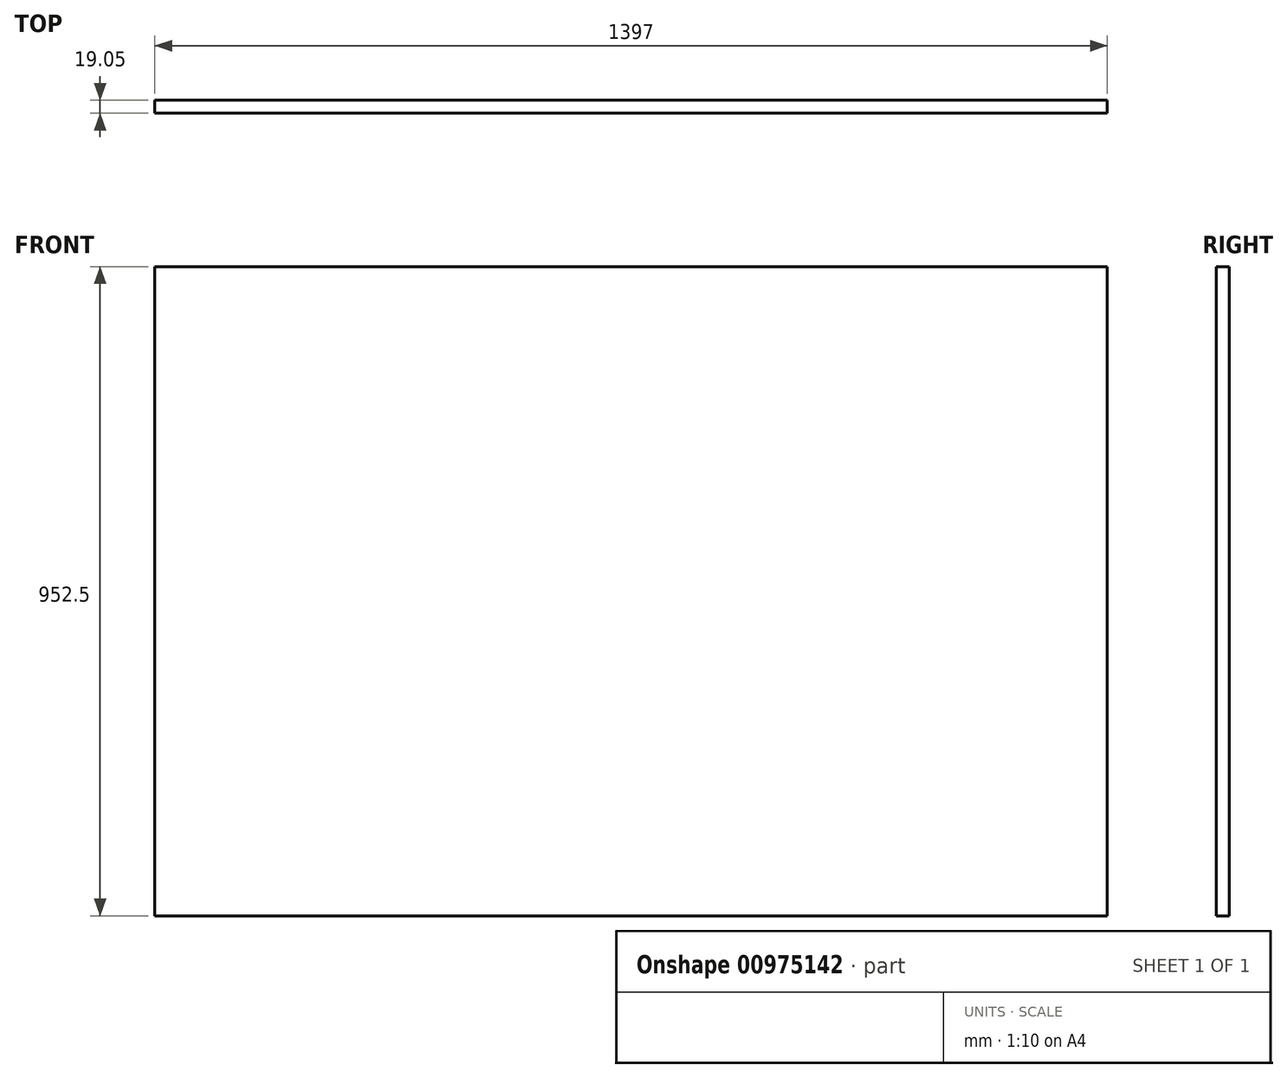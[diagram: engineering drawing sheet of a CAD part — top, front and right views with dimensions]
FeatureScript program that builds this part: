
annotation { "Feature Type Name" : "Feature", "Feature Type Description" : "" }
export const myFeature = defineFeature(function(context is Context, id is Id, definition is map)
    precondition{}
    {
        {
            var Q0;
            Q0=qCreatedBy(makeId("Front.planeOp"),FACE);
            var sketch = newSketch(context, id + "F0", { "sketchPlane" : qUnion([Q0])});
            skLineSegment(sketch, "E0.bottom", {"start": v(0, 0) * mm, "end": v(1397, 0) * mm});
            skLineSegment(sketch, "E0.top", {"start": v(0, 952.5) * mm, "end": v(1397, 952.5) * mm});
            skLineSegment(sketch, "E0.left", {"start": v(0, 0) * mm, "end": v(0, 952.5) * mm});
            skLineSegment(sketch, "E0.right", {"start": v(1397, 0) * mm, "end": v(1397, 952.5) * mm});
            skSolve(sketch);
        }
        {
            var Q0;
            Q0=makeQuery(id+"F0.imprint","IMPRINT",FACE,{"disambiguationData":[TD([[makeQuery(id+"F0.imprint","IMPRINT",EDGE,{"derivedFrom":sQuery(id+"F0.wireOp",EDGE,"E0.bottom")}),1.0]])]});
            extrude(context, id + "F1", {"entities" : qUnion([Q0]), "depth" : 19.05 * mm, "offsetDistance" : 25.4 * mm});
        }
    });
